# Revit family: PRD_FrankeWS_WtrSplySystmsCtrl_CoinOperatedController_AQUA802
name_source: partatom
category: Electrical Equipment
revit_build: Autodesk Revit 2018 (Build: 20190510_1515(x64)
units: mm (PartAtom-declared; Revit-internal decimal feet)

## family parameters
Cut with Voids When Loaded = No
Host = Face
OmniClass Number = 23.45.55.11
OmniClass Title = Sanitary Components
Part Type = Equipment Switch
Room Calculation Point = No
Round Connector Dimension = Use Diameter
Shared = No

## types (1)
- AQUA802
    AssetType = Fixed
    BIMObjectName = PRD_AR_WaterSupplySystemsControl_CoinOperatedController_AQUA802
    Category = Ss_75_70_52_96, Water supply control systems
    ControllerMaterial = PRD_AR_StainlessSteel_SatinFinished
    Default Elevation = 1500 mm  [stored 4.92126 ft]
    Description = AQUAPAY coin-operated controller for chargeable water delivery for controlling 2 - 31 A3000 open shower fittings. Display for user guide and showing free showers, selectable via key. Shower duration for one token is selectable in steps of one second up to a total of 8 minutes, preset to 3 minutes. Automatic interruption of shower-duration when water is not being withdrawn. Rugged stainless steel housing for on-wall mounting with safety lock. 24 V DC. for tokens
    DurationUnit = year
    ElectricalDeviceNominalPower = 10 VA
    GrossWeight = 3.97 kg
    HasProtectiveEarth = Yes
    IP_Code = 22
    IfcExportAs = IfcDistributionElement
    IfcExportType = NOTDEFINED
    InsulationStandardClass = NotKnown
    Manufacturer = KWC Group AG
    ManufacturerName = KWC Group AG
    ManufacturerURL = www.kwc.com
    Model = AQUA802
    ModelNumber = 2000100418
    ModelReference = AQUA802
    NBSDescription = Water supply systems control
    NBSReference = 75-75-50/110
    Name = Coin-operated controller AQUA802
    NetWeight = 3.53 kg
    NominalCurrent = 0 A
    NominalFrequencyRange = 50
    NominalHeight = 220 mm  [stored 0.721785 ft]
    NominalLength = 130 mm  [stored 0.426509 ft]
    NominalVoltage = 24
    NominalWidth = 240 mm  [stored 0.787402 ft]
    NumberOfPoles = 1
    PhaseAngle = 0.00°
    PhaseReference = 0
    ProductInformation = https://pim.kwc.com
    SecondMaterial = <By Category>
    Size = 240x220x130 mm
    URL = www.kwc.com
    Uniclass2015Code = Ss_75_70_52_96
    Uniclass2015Title = Water supply control systems
    Uniclass2015Version = Systems v1.7
    UsageCurrent = 0 A
    Version = 1
    Voltage = 24
    WarrantyDurationUnit = year

note: [stored X ft] marks values corroborated as IEEE doubles in the binary element streams (Revit-internal decimal feet)

## geometry (parser evidence)
native form markers: Sweep x2
no freeform markers — native parametric forms only
